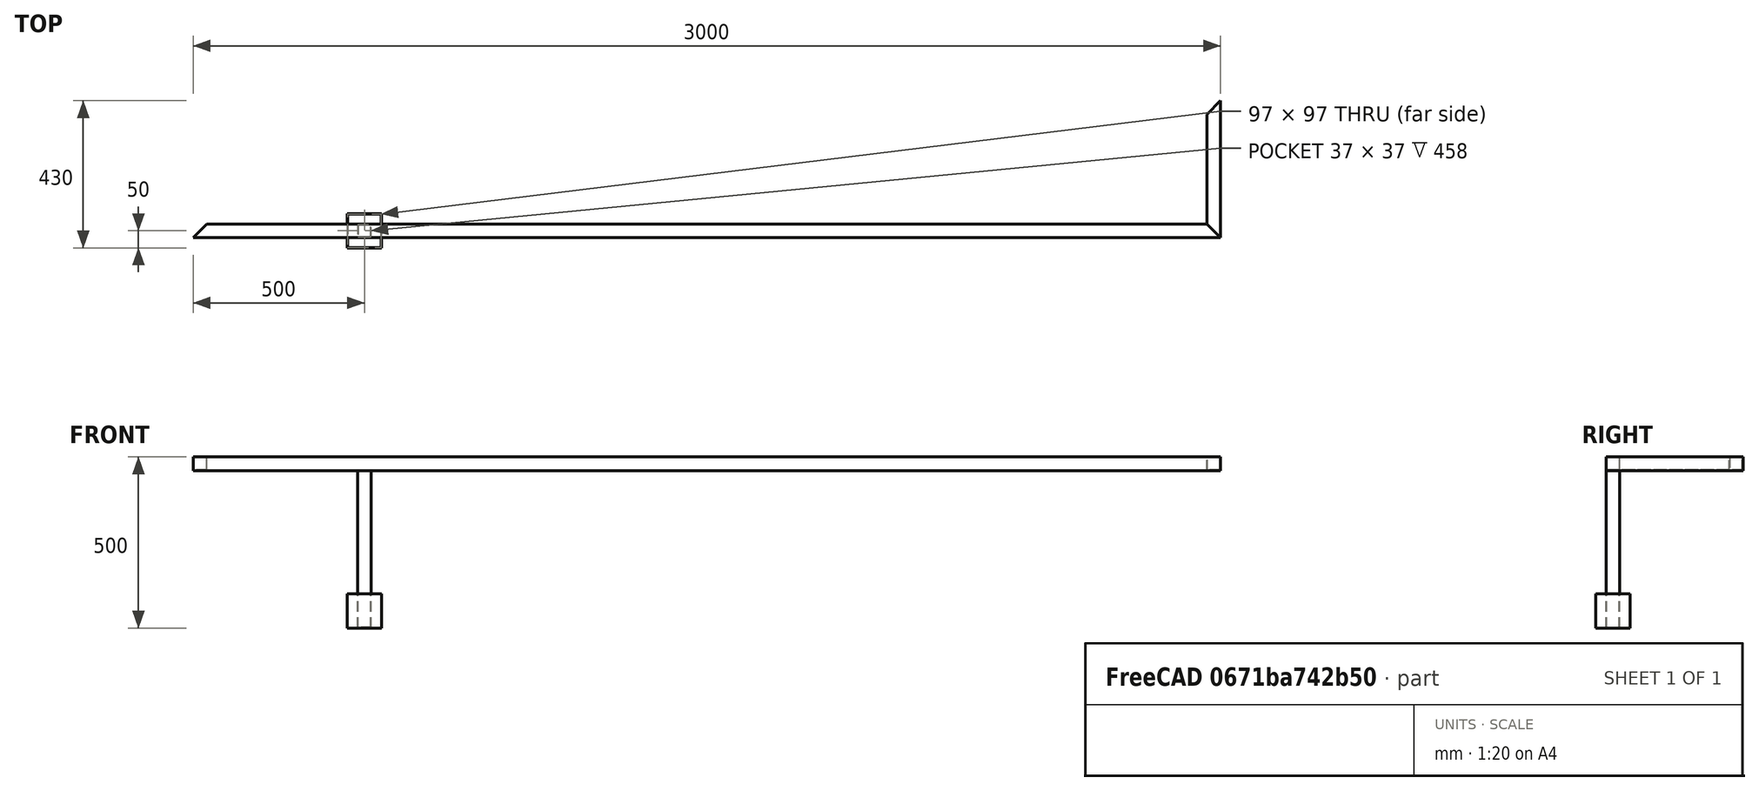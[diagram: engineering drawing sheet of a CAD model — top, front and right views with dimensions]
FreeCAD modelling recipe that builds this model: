
FCSTD DOCUMENT  (FreeCAD 0.19R)
Label: podstavek
License: All rights reserved
LicenseURL: http://en.wikipedia.org/wiki/All_rights_reserved
objects: PartDesign::CoordinateSystem×12, App::Link×8, TechDraw::DrawViewDimension×8, Sketcher::SketchObject×7, PartDesign::Pad×5, App::Part×4, App::DocumentObjectGroup×3, PartDesign::Body×3, PartDesign::Pocket×2, TechDraw::DrawViewPart×2, App::FeaturePython×1, TechDraw::DrawSVGTemplate×1, TechDraw::DrawViewSection×1, TechDraw::DrawViewAnnotation×1, TechDraw::DrawPage×1
note: 36 computed .brp shape members not serialized (recipe doc carries the construction recipe); baked Part::Feature solids carry a one-line shape summary decoded from their .brp

FEATURE [PartDesign::CoordinateSystem] LCS_Origin
  AttacherType = Attacher::AttachEngine3D
  MapMode = 2
  Support = -> [X_Axis]
FEATURE [App::FeaturePython] Variables  # WARN: FeaturePython — macro-defined, semantics opaque (R4)
  Type = App::PropertyContainer
  beam_thickness = 1.5
  beam_width = 40
  depth = 400
  height = 500
  length = 3000
FEATURE [App::DocumentObjectGroup] Constraints
FEATURE [App::DocumentObjectGroup] Configurations
FEATURE [PartDesign::CoordinateSystem] LCS_0
  AttacherType = Attacher::AttachEngine3D
  MapMode = 2
  Support = -> [X_Axis001]
FEATURE [PartDesign::CoordinateSystem] LCS_0001
  AttacherType = Attacher::AttachEngine3D
  MapMode = 2
  Support = -> [X_Axis002]
FEATURE [Sketcher::SketchObject] Sketch
  FullyConstrained = true
  MapMode = 5
  Placement = pos=(0,0,0) rot=(0.57735,0.57735,0.57735;2.0944rad)
  Support = -> [YZ_Plane002]
  expr: Constraints[27] = Variables.depth / 2
  expr: Constraints[28] = Variables.height
  sketch-geometry (10):
    g0: LineSegment StartX=-160 StartY=460 StartZ=0 EndX=-160 EndY=500 EndZ=0
    g1: LineSegment StartX=-160 StartY=500 StartZ=0 EndX=-200 EndY=500 EndZ=0
    g2: LineSegment StartX=-200 StartY=500 StartZ=0 EndX=-200 EndY=460 EndZ=0
    g3: LineSegment StartX=-200 StartY=460 StartZ=0 EndX=-160 EndY=460 EndZ=0
    g4: Circle CenterX=-180 CenterY=480 CenterZ=0 NormalX=0 NormalY=0 NormalZ=1 AngleXU=0 Radius=28.2843
    g5: LineSegment StartX=-198.5 StartY=461.5 StartZ=0 EndX=-161.5 EndY=461.5 EndZ=0
    g6: LineSegment StartX=-161.5 StartY=461.5 StartZ=0 EndX=-161.5 EndY=498.5 EndZ=0
    g7: LineSegment StartX=-161.5 StartY=498.5 StartZ=0 EndX=-198.5 EndY=498.5 EndZ=0
    g8: LineSegment StartX=-198.5 StartY=498.5 StartZ=0 EndX=-198.5 EndY=461.5 EndZ=0
    g9: Circle CenterX=-180 CenterY=480 CenterZ=0 NormalX=0 NormalY=0 NormalZ=1 AngleXU=0 Radius=26.163
  constraints (29):
    c: Coincident(g0,g1)
    c: Coincident(g1,g2)
    c: Coincident(g2,g3)
    c: Coincident(g3,g0)
    c: Equal(g0,g1)
    c: Equal(g0,g2)
    c: Equal(g0,g3)
    c: PointOnObject(g0,g4)
    c: PointOnObject(g1,g4)
    c: PointOnObject(g2,g4)
    c: PointOnObject(g3,g4)
    c: Coincident(g5,g6)
    c: Coincident(g6,g7)
    c: Coincident(g7,g8)
    c: Coincident(g8,g5)
    c: Equal(g5,g6)
    c: Equal(g5,g7)
    c: Equal(g5,g8)
    c: PointOnObject(g5,g9)
    c: PointOnObject(g6,g9)
    c: PointOnObject(g7,g9)
    c: PointOnObject(g8,g9)
    c: Coincident(g9,g4)
    c: Horizontal(g3)
    c: Horizontal(g5)
    c: DistanceY(g0,g5) = 1.5  's'
    c: DistanceY(g0,g0) = 40
    c: DistanceX(g2,g-1) = 200
    c: DistanceY(g-1,g1) = 500
FEATURE [PartDesign::Pad] Pad
  Direction = (1,1,1)
  Length = 3000
  Length2 = 100
  Midplane = true
  Placement = pos=(0,0,0) rot=(0.57735,0.57735,0.57735;2.0944rad)
  Profile = -> Sketch
  Type = 0
  expr: Length = Variables.length
FEATURE [Sketcher::SketchObject] Sketch001
  ExternalGeometry = -> [Pad]
  FullyConstrained = true
  MapMode = 5
  Support = -> [XY_Plane002]
  sketch-geometry (6):
    g0: LineSegment StartX=-1500 StartY=-200 StartZ=0 EndX=-1460 EndY=-160 EndZ=0
    g1: LineSegment StartX=-1460 StartY=-160 StartZ=0 EndX=-1500 EndY=-160 EndZ=0
    g2: LineSegment StartX=-1500 StartY=-160 StartZ=0 EndX=-1500 EndY=-200 EndZ=0
    g3: LineSegment StartX=1500 StartY=-160 StartZ=0 EndX=1500 EndY=-200 EndZ=0
    g4: LineSegment StartX=1500 StartY=-160 StartZ=0 EndX=1460 EndY=-160 EndZ=0
    g5: LineSegment StartX=1460 StartY=-160 StartZ=0 EndX=1500 EndY=-200 EndZ=0
  constraints (14):
    c: Coincident(g0,g1)
    c: Horizontal(g1)
    c: Coincident(g1,g2)
    c: Equal(g2,g1)
    c: Coincident(g1,g-3)
    c: Coincident(g0,g2)
    c: Coincident(g0,g-3)
    c: Coincident(g3,g4)
    c: Horizontal(g4)
    c: Coincident(g4,g5)
    c: Coincident(g5,g3)
    c: Equal(g3,g4)
    c: Coincident(g3,g-4)
    c: Coincident(g3,g-4)
FEATURE [PartDesign::Pocket] Pocket
  BaseFeature = -> Pad
  Length = 5
  Length2 = 100
  Placement = pos=(0,0,0) rot=(0.57735,0.57735,0.57735;2.0944rad)
  Profile = -> Sketch001
  Reversed = true
  Type = 1
FEATURE [PartDesign::Body] Body
  Group = -> [LCS_0001,Sketch,Pad,Sketch001,Pocket]
  Origin = -> Origin002
  Tip = -> Pocket
FEATURE [App::Part] frame  label="frame_beam_1"
  Group = -> [LCS_0,Body]
  Origin = -> Origin001
FEATURE [PartDesign::CoordinateSystem] LCS_0002
  AttacherType = Attacher::AttachEngine3D
  MapMode = 2
  Support = -> [X_Axis003]
FEATURE [PartDesign::CoordinateSystem] LCS_0003
  AttacherType = Attacher::AttachEngine3D
  MapMode = 2
  Support = -> [X_Axis004]
FEATURE [Sketcher::SketchObject] Sketch002
  FullyConstrained = true
  MapMode = 5
  Placement = pos=(0,0,0) rot=(1,0,0;1.5708rad)
  Support = -> [XZ_Plane004]
  expr: Constraints[25] = Variables.beam_thickness
  expr: Constraints[28] = Variables.length / 2
  expr: Constraints[26] = Variables.beam_width
  expr: Constraints[27] = Variables.height
  sketch-geometry (10):
    g0: LineSegment StartX=1500 StartY=500 StartZ=0 EndX=1460 EndY=500 EndZ=0
    g1: LineSegment StartX=1460 StartY=500 StartZ=0 EndX=1460 EndY=460 EndZ=0
    g2: LineSegment StartX=1460 StartY=460 StartZ=0 EndX=1500 EndY=460 EndZ=0
    g3: LineSegment StartX=1500 StartY=460 StartZ=0 EndX=1500 EndY=500 EndZ=0
    g4: Circle CenterX=1480 CenterY=480 CenterZ=0 NormalX=0 NormalY=0 NormalZ=1 AngleXU=0 Radius=28.2843
    g5: LineSegment StartX=1498.5 StartY=498.5 StartZ=0 EndX=1461.5 EndY=498.5 EndZ=0
    g6: LineSegment StartX=1461.5 StartY=498.5 StartZ=0 EndX=1461.5 EndY=461.5 EndZ=0
    g7: LineSegment StartX=1461.5 StartY=461.5 StartZ=0 EndX=1498.5 EndY=461.5 EndZ=0
    g8: LineSegment StartX=1498.5 StartY=461.5 StartZ=0 EndX=1498.5 EndY=498.5 EndZ=0
    g9: Circle CenterX=1480 CenterY=480 CenterZ=0 NormalX=0 NormalY=0 NormalZ=1 AngleXU=0 Radius=26.163
  constraints (29):
    c: Coincident(g0,g1)
    c: Coincident(g1,g2)
    c: Coincident(g2,g3)
    c: Coincident(g3,g0)
    c: Equal(g0,g1)
    c: Equal(g0,g2)
    c: Equal(g0,g3)
    c: PointOnObject(g0,g4)
    c: PointOnObject(g1,g4)
    c: PointOnObject(g2,g4)
    c: PointOnObject(g3,g4)
    c: Coincident(g5,g6)
    c: Coincident(g6,g7)
    c: Coincident(g7,g8)
    c: Coincident(g8,g5)
    c: Equal(g5,g6)
    c: Equal(g5,g7)
    c: Equal(g5,g8)
    c: PointOnObject(g5,g9)
    c: PointOnObject(g6,g9)
    c: PointOnObject(g7,g9)
    c: PointOnObject(g8,g9)
    c: Coincident(g9,g4)
    c: Horizontal(g7)
    c: Horizontal(g2)
    c: DistanceY(g2,g7) = 1.5
    c: DistanceY(g3,g3) = 40
    c: DistanceY(g-1,g0) = 500
    c: DistanceX(g-1,g2) = 1500
FEATURE [PartDesign::Pad] Pad001
  Direction = (1,1,1)
  Length = 400
  Length2 = 100
  Midplane = true
  Placement = pos=(0,0,0) rot=(1,0,0;1.5708rad)
  Profile = -> Sketch002
  Type = 0
  expr: Length = Variables.depth
FEATURE [Sketcher::SketchObject] Sketch003
  ExternalGeometry = -> [Pad001]
  FullyConstrained = true
  MapMode = 5
  Support = -> [XY_Plane004]
  sketch-geometry (6):
    g0: LineSegment StartX=1460 StartY=200 StartZ=0 EndX=1500 EndY=200 EndZ=0
    g1: LineSegment StartX=1500 StartY=200 StartZ=0 EndX=1460 EndY=160 EndZ=0
    g2: LineSegment StartX=1460 StartY=160 StartZ=0 EndX=1460 EndY=200 EndZ=0
    g3: LineSegment StartX=1460 StartY=-200 StartZ=0 EndX=1460 EndY=-160 EndZ=0
    g4: LineSegment StartX=1460 StartY=-160 StartZ=0 EndX=1500 EndY=-200 EndZ=0
    g5: LineSegment StartX=1500 StartY=-200 StartZ=0 EndX=1460 EndY=-200 EndZ=0
  constraints (14):
    c: Coincident(g0,g1)
    c: Coincident(g1,g2)
    c: Coincident(g2,g0)
    c: Vertical(g3)
    c: Coincident(g3,g4)
    c: Coincident(g4,g5)
    c: Coincident(g5,g3)
    c: Vertical(g2)
    c: Equal(g2,g0)
    c: Equal(g3,g5)
    c: Coincident(g3,g-4)
    c: Coincident(g4,g-4)
    c: Coincident(g0,g-3)
    c: Coincident(g0,g-3)
FEATURE [PartDesign::Pocket] Pocket001
  BaseFeature = -> Pad001
  Length = 5
  Length2 = 100
  Placement = pos=(0,0,0) rot=(1,0,0;1.5708rad)
  Profile = -> Sketch003
  Reversed = true
  Type = 1
FEATURE [PartDesign::Body] Body_2
  Group = -> [LCS_0003,Sketch002,Pad001,Sketch003,Pocket001]
  Origin = -> Origin004
  Tip = -> Pocket001
FEATURE [App::Part] frame_beam_2
  Group = -> [LCS_0002,Body_2]
  Origin = -> Origin003
FEATURE [App::Link] frame_beam_1  label="frame_beam_front"
  AssemblyType = Part::Link
  AttachedBy = #LCS_0
  AttachedTo = Parent Assembly#LCS_Origin
  LinkedObject = -> frame
  SolverId = Asm4EE
  expr: Placement = LCS_Origin.Placement * AttachmentOffset * LCS_0.Placement ^ -1
FEATURE [App::Link] frame_beam  label="frame_beam_rear"
  AssemblyType = Part::Link
  AttachedBy = #LCS_0
  AttachedTo = Parent Assembly#LCS_Origin
  AttachmentOffset = pos=(0,0,0) rot=(0,0,1;3.14159rad)
  LinkPlacement = pos=(0,0,0) rot=(0,0,1;3.14159rad)
  LinkedObject = -> frame
  Placement = pos=(0,0,0) rot=(0,0,1;3.14159rad)
  SolverId = Asm4EE
  expr: Placement = LCS_Origin.Placement * AttachmentOffset * LCS_0.Placement ^ -1
FEATURE [App::Link] frame_beam_2001  label="frame_beam_right"
  AssemblyType = Part::Link
  AttachedBy = #LCS_0002
  AttachedTo = Parent Assembly#LCS_Origin
  LinkedObject = -> frame_beam_2
  SolverId = Asm4EE
  expr: Placement = LCS_Origin.Placement * AttachmentOffset * LCS_0002.Placement ^ -1
FEATURE [App::Link] frame_beam_3  label="frame_beam_left"
  AssemblyType = Part::Link
  AttachedBy = #LCS_0002
  AttachedTo = Parent Assembly#LCS_Origin
  AttachmentOffset = pos=(0,0,0) rot=(0,0,1;3.14159rad)
  LinkPlacement = pos=(0,0,0) rot=(0,0,1;3.14159rad)
  LinkedObject = -> frame_beam_2
  Placement = pos=(0,0,0) rot=(0,0,1;3.14159rad)
  SolverId = Asm4EE
  expr: Placement = LCS_Origin.Placement * AttachmentOffset * LCS_0002.Placement ^ -1
FEATURE [PartDesign::CoordinateSystem] LCS_0004
  AttacherType = Attacher::AttachEngine3D
  MapMode = 2
  Support = -> [X_Axis005]
FEATURE [PartDesign::CoordinateSystem] LCS_0005
  AttacherType = Attacher::AttachEngine3D
  MapMode = 2
  Support = -> [X_Axis006]
FEATURE [Sketcher::SketchObject] Sketch004
  FullyConstrained = true
  MapMode = 5
  Support = -> [XY_Plane006]
  expr: Constraints[14] = (Variables.depth - Variables.beam_width) / 2
  expr: Constraints[13] = Variables.length / 3
  sketch-geometry (5):
    g0: LineSegment StartX=-950 StartY=-130 StartZ=0 EndX=-1050 EndY=-130 EndZ=0
    g1: LineSegment StartX=-1050 StartY=-130 StartZ=0 EndX=-1050 EndY=-230 EndZ=0
    g2: LineSegment StartX=-1050 StartY=-230 StartZ=0 EndX=-950 EndY=-230 EndZ=0
    g3: LineSegment StartX=-950 StartY=-230 StartZ=0 EndX=-950 EndY=-130 EndZ=0
    g4: Circle CenterX=-1000 CenterY=-180 CenterZ=0 NormalX=0 NormalY=0 NormalZ=1 AngleXU=0 Radius=70.7107
  constraints (15):
    c: Coincident(g0,g1)
    c: Coincident(g1,g2)
    c: Coincident(g2,g3)
    c: Coincident(g3,g0)
    c: Equal(g0,g1)
    c: Equal(g0,g2)
    c: Equal(g0,g3)
    c: PointOnObject(g0,g4)
    c: PointOnObject(g1,g4)
    c: PointOnObject(g2,g4)
    c: PointOnObject(g3,g4)
    c: Horizontal(g2)
    c: DistanceX(g2,g2) = 100
    c: DistanceX(g4,g-1) = 1000
    c: DistanceY(g4,g-1) = 180
FEATURE [PartDesign::Pad] Pad002
  Direction = (1,1,1)
  Length = 2
  Length2 = 100
  Profile = -> Sketch004
  Type = 0
FEATURE [Sketcher::SketchObject] Sketch005
  ExternalGeometry = -> [Pad002]
  FullyConstrained = true
  MapMode = 5
  Placement = pos=(0,0,2) rot=(0,0,1;0rad)
  Support = -> [Pad002,XY_Plane]
  expr: Constraints[30] = Variables.beam_thickness
  expr: Constraints[29] = Variables.beam_width
  sketch-geometry (11):
    g0: LineSegment StartX=-980 StartY=-160 StartZ=0 EndX=-1020 EndY=-160 EndZ=0
    g1: LineSegment StartX=-1020 StartY=-160 StartZ=0 EndX=-1020 EndY=-200 EndZ=0
    g2: LineSegment StartX=-1020 StartY=-200 StartZ=0 EndX=-980 EndY=-200 EndZ=0
    g3: LineSegment StartX=-980 StartY=-200 StartZ=0 EndX=-980 EndY=-160 EndZ=0
    g4: Circle CenterX=-1000 CenterY=-180 CenterZ=0 NormalX=0 NormalY=0 NormalZ=1 AngleXU=0 Radius=28.2843
    g5: LineSegment StartX=-981.5 StartY=-161.5 StartZ=0 EndX=-1018.5 EndY=-161.5 EndZ=0
    g6: LineSegment StartX=-1018.5 StartY=-161.5 StartZ=0 EndX=-1018.5 EndY=-198.5 EndZ=0
    g7: LineSegment StartX=-1018.5 StartY=-198.5 StartZ=0 EndX=-981.5 EndY=-198.5 EndZ=0
    g8: LineSegment StartX=-981.5 StartY=-198.5 StartZ=0 EndX=-981.5 EndY=-161.5 EndZ=0
    g9: Circle CenterX=-1000 CenterY=-180 CenterZ=0 NormalX=0 NormalY=0 NormalZ=1 AngleXU=0 Radius=26.163
    g10: Circle CenterX=-1000 CenterY=-180 CenterZ=0 NormalX=0 NormalY=0 NormalZ=1 AngleXU=0 Radius=70.7107
  constraints (31):
    c: Coincident(g0,g1)
    c: Coincident(g1,g2)
    c: Coincident(g2,g3)
    c: Coincident(g3,g0)
    c: Equal(g0,g1)
    c: Equal(g0,g2)
    c: Equal(g0,g3)
    c: PointOnObject(g0,g4)
    c: PointOnObject(g1,g4)
    c: PointOnObject(g2,g4)
    c: PointOnObject(g3,g4)
    c: Coincident(g5,g6)
    c: Coincident(g6,g7)
    c: Coincident(g7,g8)
    c: Coincident(g8,g5)
    c: Equal(g5,g6)
    c: Equal(g5,g7)
    c: Equal(g5,g8)
    c: PointOnObject(g5,g9)
    c: PointOnObject(g6,g9)
    c: PointOnObject(g7,g9)
    c: PointOnObject(g8,g9)
    c: Coincident(g9,g4)
    c: Coincident(g10,g4)
    c: PointOnObject(g-3,g10)
    c: PointOnObject(g-4,g10)
    c: PointOnObject(g-4,g10)
    c: Horizontal(g7)
    c: Horizontal(g2)
    c: DistanceY(g3,g3) = 40
    c: DistanceY(g2,g7) = 1.5
FEATURE [PartDesign::Pad] Pad003
  BaseFeature = -> Pad002
  Direction = (1,1,1)
  Length = 458
  Length2 = 100
  Profile = -> Sketch005
  Type = 0
  expr: Length = Variables.height - Variables.beam_width - 2
FEATURE [Sketcher::SketchObject] Sketch006
  ExternalGeometry = -> [Pad003]
  FullyConstrained = true
  MapMode = 5
  Support = -> [XY_Plane006]
  expr: Constraints[16] = Variables.beam_thickness
  sketch-geometry (10):
    g0: LineSegment StartX=-951.5 StartY=-131.5 StartZ=0 EndX=-1048.5 EndY=-131.5 EndZ=0
    g1: LineSegment StartX=-1048.5 StartY=-131.5 StartZ=0 EndX=-1048.5 EndY=-228.5 EndZ=0
    g2: LineSegment StartX=-1048.5 StartY=-228.5 StartZ=0 EndX=-951.5 EndY=-228.5 EndZ=0
    g3: LineSegment StartX=-951.5 StartY=-228.5 StartZ=0 EndX=-951.5 EndY=-131.5 EndZ=0
    g4: Circle CenterX=-1000 CenterY=-180 CenterZ=0 NormalX=0 NormalY=0 NormalZ=1 AngleXU=0 Radius=68.5894
    g5: Circle CenterX=-1000 CenterY=-180 CenterZ=0 NormalX=0 NormalY=0 NormalZ=1 AngleXU=0 Radius=70.7107
    g6: LineSegment StartX=-1050 StartY=-130 StartZ=0 EndX=-950 EndY=-130 EndZ=0
    g7: LineSegment StartX=-950 StartY=-130 StartZ=0 EndX=-950 EndY=-230 EndZ=0
    g8: LineSegment StartX=-950 StartY=-230 StartZ=0 EndX=-1050 EndY=-230 EndZ=0
    g9: LineSegment StartX=-1050 StartY=-130 StartZ=0 EndX=-1050 EndY=-230 EndZ=0
  constraints (25):
    c: Coincident(g0,g1)
    c: Coincident(g1,g2)
    c: Coincident(g2,g3)
    c: Coincident(g3,g0)
    c: Equal(g0,g1)
    c: Equal(g0,g2)
    c: Equal(g0,g3)
    c: PointOnObject(g0,g4)
    c: PointOnObject(g1,g4)
    c: PointOnObject(g2,g4)
    c: PointOnObject(g3,g4)
    c: Horizontal(g2)
    c: Coincident(g5,g4)
    c: PointOnObject(g-5,g5)
    c: PointOnObject(g-4,g5)
    c: PointOnObject(g-6,g5)
    c: DistanceY(g0,g-5) = 1.5
    c: Coincident(g-4,g6)
    c: Coincident(g6,g-5)
    c: Coincident(g6,g7)
    c: Coincident(g7,g-6)
    c: Coincident(g7,g8)
    c: Coincident(g8,g-6)
    c: Coincident(g9,g6)
    c: Coincident(g9,g8)
FEATURE [PartDesign::Pad] Pad004
  BaseFeature = -> Pad003
  Direction = (1,1,1)
  Length = 100
  Length2 = 100
  Profile = -> Sketch006
  Type = 0
FEATURE [PartDesign::Body] Body_3
  Group = -> [LCS_0005,Sketch004,Pad002,Sketch005,Pad003,Sketch006,Pad004]
  Origin = -> Origin006
  Tip = -> Pad004
FEATURE [PartDesign::CoordinateSystem] LCS_1
  AttacherType = Attacher::AttachEngine3D
  Placement = pos=(-2000,0,0) rot=(0,0,1;0rad)
  expr: .Placement.Base.x = -(Variables.length / 3 * 2)
FEATURE [App::Part] leg
  Group = -> [LCS_0004,Body_3,LCS_1]
  Origin = -> Origin005
FEATURE [App::DocumentObjectGroup] Parts
  Group = -> [frame,frame_beam_2,leg]
FEATURE [App::Link] leg001  label="leg_1"
  AssemblyType = Part::Link
  AttachedBy = #LCS_0004
  AttachedTo = Parent Assembly#LCS_Origin
  LinkedObject = -> leg
  SolverId = Asm4EE
  expr: Placement = LCS_Origin.Placement * AttachmentOffset * LCS_0004.Placement ^ -1
FEATURE [App::Link] leg_2
  AssemblyType = Part::Link
  AttachedBy = #LCS_1
  AttachedTo = Parent Assembly#LCS_Origin
  LinkPlacement = pos=(2000,0,0) rot=(0,0,1;0rad)
  LinkedObject = -> leg
  Placement = pos=(2000,0,0) rot=(0,0,1;0rad)
  SolverId = Asm4EE
  expr: Placement = LCS_Origin.Placement * AttachmentOffset * LCS_1.Placement ^ -1
FEATURE [App::Link] leg_3
  AssemblyType = Part::Link
  AttachedBy = #LCS_0004
  AttachedTo = Parent Assembly#LCS_Origin
  AttachmentOffset = pos=(0,0,0) rot=(0,0,1;3.14159rad)
  LinkPlacement = pos=(0,0,0) rot=(0,0,1;3.14159rad)
  LinkedObject = -> leg
  Placement = pos=(0,0,0) rot=(0,0,1;3.14159rad)
  SolverId = Asm4EE
  expr: Placement = LCS_Origin.Placement * AttachmentOffset * LCS_0004.Placement ^ -1
FEATURE [App::Link] leg_4
  AssemblyType = Part::Link
  AttachedBy = #LCS_1
  AttachedTo = Parent Assembly#LCS_Origin
  AttachmentOffset = pos=(0,0,0) rot=(0,0,1;3.14159rad)
  LinkPlacement = pos=(-2000,2.449e-13,0) rot=(0,0,1;3.14159rad)
  LinkedObject = -> leg
  Placement = pos=(-2000,2.449e-13,0) rot=(0,0,1;3.14159rad)
  SolverId = Asm4EE
  expr: Placement = LCS_Origin.Placement * AttachmentOffset * LCS_1.Placement ^ -1
FEATURE [TechDraw::DrawSVGTemplate] Template
  EditableTexts = AVTOR=Brane Borštnik; AVTOR_2=Risal: Janez Paternoster; DATUM=6.5.2022; MATERIAL=inox; MERILO=1:5; NAZIV=Podstavek; NAZIV_2=Dadant-Blatt panj; STRAN=Stran 1/1; VIR=https://github.com/<owner>/Dadant-Blatt
  Height = 210
  Orientation = 1
  Width = 297
FEATURE [TechDraw::DrawViewPart] View001
  CoarseView = false
  Direction = (0,0,1)
  Focus = 100
  HardHidden = false
  IsoCount = 0
  IsoHidden = false
  IsoVisible = false
  LockPosition = false
  Perspective = false
  Rotation = 0
  Scale = 0.2
  ScaleType = 0
  SeamHidden = false
  SeamVisible = true
  SmoothHidden = false
  SmoothVisible = true
  Source = -> [leg]
  X = 38.9871
  XDirection = (1,0,0)
  Y = 55
FEATURE [TechDraw::DrawViewSection] SectionView  label="Section A - A"
  BaseView = -> View001
  CoarseView = false
  CutSurfaceDisplay = 2
  Direction = (-1,0,0)
  FileGeomPattern = <path>
  FileHatchPattern = <path>
  Focus = 100
  FuseBeforeCut = false
  HardHidden = false
  HatchScale = 1
  IsoCount = 0
  IsoHidden = false
  IsoVisible = false
  LockPosition = false
  NameGeomPattern = Diamant
  Perspective = false
  Rotation = 0
  Scale = 0.2
  ScaleType = 0
  SeamHidden = false
  SeamVisible = true
  SectionDirection = 0
  SectionNormal = (-1,0,0)
  SectionOrigin = (-1000,-180,231)
  SectionSymbol = A
  SmoothHidden = false
  SmoothVisible = true
  Source = -> [leg]
  X = 137.492
  XDirection = (0,0,1)
  Y = 55
FEATURE [TechDraw::DrawViewDimension] Dimension003
  Arbitrary = false
  ArbitraryTolerances = false
  EqualTolerance = true
  FormatSpec = cev ▫%.6g
  FormatSpecOverTolerance = %+.6g
  FormatSpecUnderTolerance = %+.6g
  Inverted = false
  LockPosition = false
  MeasureType = 1
  OverTolerance = 0
  References2D = -> [SectionView]
  Rotation = 0
  Scale = 0.1
  ScaleType = 0
  TheoreticalExact = false
  Type = 2
  UnderTolerance = 0
  X = 61.402
  Y = 16.0323
FEATURE [TechDraw::DrawViewDimension] Dimension004
  Arbitrary = false
  ArbitraryTolerances = false
  EqualTolerance = true
  FormatSpec = cev ▫%.6g
  FormatSpecOverTolerance = %+.6g
  FormatSpecUnderTolerance = %+.6g
  Inverted = false
  LockPosition = false
  MeasureType = 1
  OverTolerance = 0
  References2D = -> [SectionView]
  Rotation = 0
  Scale = 0.1
  ScaleType = 0
  TheoreticalExact = false
  Type = 2
  UnderTolerance = 0
  X = 52.742
  Y = 21.9335
FEATURE [TechDraw::DrawViewDimension] Dimension005
  Arbitrary = false
  ArbitraryTolerances = false
  EqualTolerance = true
  FormatSpec = %.6g
  FormatSpecOverTolerance = %+.6g
  FormatSpecUnderTolerance = %+.6g
  Inverted = false
  LockPosition = false
  MeasureType = 1
  OverTolerance = 0
  References2D = -> [SectionView]
  Rotation = 0
  Scale = 0.1
  ScaleType = 0
  TheoreticalExact = false
  Type = 1
  UnderTolerance = 0
  X = -35.6122
  Y = 25.9891
FEATURE [TechDraw::DrawViewDimension] Dimension006
  Arbitrary = false
  ArbitraryTolerances = false
  EqualTolerance = true
  FormatSpec = %.6g
  FormatSpecOverTolerance = %+.6g
  FormatSpecUnderTolerance = %+.6g
  Inverted = false
  LockPosition = false
  MeasureType = 1
  OverTolerance = 0
  References2D = -> [SectionView]
  Rotation = 0
  Scale = 0.1
  ScaleType = 0
  TheoreticalExact = false
  Type = 1
  UnderTolerance = 0
  X = -1.10007
  Y = 39.0791
FEATURE [TechDraw::DrawViewDimension] Dimension007
  Arbitrary = false
  ArbitraryTolerances = false
  EqualTolerance = true
  FormatSpec = %.6g (ploščica)
  FormatSpecOverTolerance = %+.6g
  FormatSpecUnderTolerance = %+.6g
  Inverted = false
  LockPosition = false
  MeasureType = 1
  OverTolerance = 0
  References2D = -> [SectionView]
  Rotation = 0
  Scale = 0.1
  ScaleType = 0
  TheoreticalExact = false
  Type = 1
  UnderTolerance = 0
  X = -62.8671
  Y = -10.604
FEATURE [TechDraw::DrawViewAnnotation] Annotation
  Font = osifont
  LineSpace = 80
  LockPosition = false
  MaxWidth = -1
  Rotation = 0
  Scale = 0.1
  ScaleType = 0
  Text = Noge imajo bazen\u010dek | proti mravljam, | Napolni se z vodo ali | oljem. Potrebno je | min. 30mm prehoda.
  TextSize = 5
  TextStyle = 0
  X = 250.551
  Y = 52.7949
FEATURE [PartDesign::CoordinateSystem] LCS_panj1
  AttacherType = Attacher::AttachEngine3D
  Placement = pos=(-900,0,500) rot=(0,0,1;0rad)
  expr: .Placement.Base.x = -900
  expr: .Placement.Base.z = Variables.height
FEATURE [PartDesign::CoordinateSystem] LCS_panj2
  AttacherType = Attacher::AttachEngine3D
  Placement = pos=(-300,0,500) rot=(0,0,1;0rad)
  expr: .Placement.Base.z = Variables.height
FEATURE [PartDesign::CoordinateSystem] LCS_panj3
  AttacherType = Attacher::AttachEngine3D
  Placement = pos=(300,0,500) rot=(0,0,1;0rad)
  expr: .Placement.Base.z = Variables.height
FEATURE [PartDesign::CoordinateSystem] LCS_panj4
  AttacherType = Attacher::AttachEngine3D
  Placement = pos=(900,0,500) rot=(0,0,1;0rad)
  expr: .Placement.Base.z = Variables.height
FEATURE [App::Part] Assembly
  AssemblyType = Part::Link
  Group = -> [LCS_Origin,Variables,Constraints,Configurations,frame_beam_1,frame_beam,frame_beam_2001,frame_beam_3,leg001,leg_2,leg_3,leg_4,LCS_panj1,LCS_panj2,LCS_panj3,LCS_panj4]
  Origin = -> Origin
  Type = Assembly
FEATURE [TechDraw::DrawViewPart] View
  CoarseView = false
  Direction = (0.333,-0.882,0.333)
  Focus = 100
  HardHidden = false
  IsoCount = 0
  IsoHidden = false
  IsoVisible = false
  LockPosition = false
  Perspective = false
  Rotation = 0
  Scale = 0.08
  ScaleType = 0
  SeamHidden = false
  SeamVisible = true
  SmoothHidden = false
  SmoothVisible = true
  Source = -> [Assembly]
  X = 141.404
  XDirection = (0.935,0.354,0)
  Y = 137.368
FEATURE [TechDraw::DrawViewDimension] Dimension001
  Arbitrary = false
  ArbitraryTolerances = false
  EqualTolerance = true
  FormatSpec = %.6g
  FormatSpecOverTolerance = %+.6g
  FormatSpecUnderTolerance = %+.6g
  Inverted = false
  LockPosition = false
  MeasureType = 0
  OverTolerance = 0
  References2D = -> [View]
  References3D = -> [Assembly]
  Rotation = 0
  Scale = 0.1
  ScaleType = 0
  TheoreticalExact = false
  Type = 0
  UnderTolerance = 0
  X = -121.286
  Y = 41.4897
FEATURE [TechDraw::DrawViewDimension] Dimension
  Arbitrary = false
  ArbitraryTolerances = false
  EqualTolerance = true
  FormatSpec = %.6g
  FormatSpecOverTolerance = %+.6g
  FormatSpecUnderTolerance = %+.6g
  Inverted = false
  LockPosition = false
  MeasureType = 0
  OverTolerance = 0
  References2D = -> [View]
  References3D = -> [Assembly]
  Rotation = 0
  Scale = 0.1
  ScaleType = 0
  TheoreticalExact = false
  Type = 0
  UnderTolerance = 0
  X = 14.0775
  Y = 35.6315
FEATURE [TechDraw::DrawViewDimension] Dimension002
  Arbitrary = false
  ArbitraryTolerances = false
  EqualTolerance = true
  FormatSpec = %.6g
  FormatSpecOverTolerance = %+.6g
  FormatSpecUnderTolerance = %+.6g
  Inverted = false
  LockPosition = false
  MeasureType = 0
  OverTolerance = 0
  References2D = -> [View]
  References3D = -> [Assembly]
  Rotation = 0
  Scale = 0.1
  ScaleType = 0
  TheoreticalExact = false
  Type = 2
  UnderTolerance = 0
  X = 128.444
  Y = -6.20312
FEATURE [TechDraw::DrawPage] Page
  KeepUpdated = true
  NextBalloonIndex = 1
  ProjectionType = 0
  Scale = 0.1
  Template = -> Template
  Views = -> [View,Dimension001,Dimension,Dimension002,View001,SectionView,Dimension003,Dimension004,Dimension005,Dimension006,Dimension007,Annotation]
note: 2 file-system paths scrubbed to <path> (originals preserved in the JSON sidecar)
